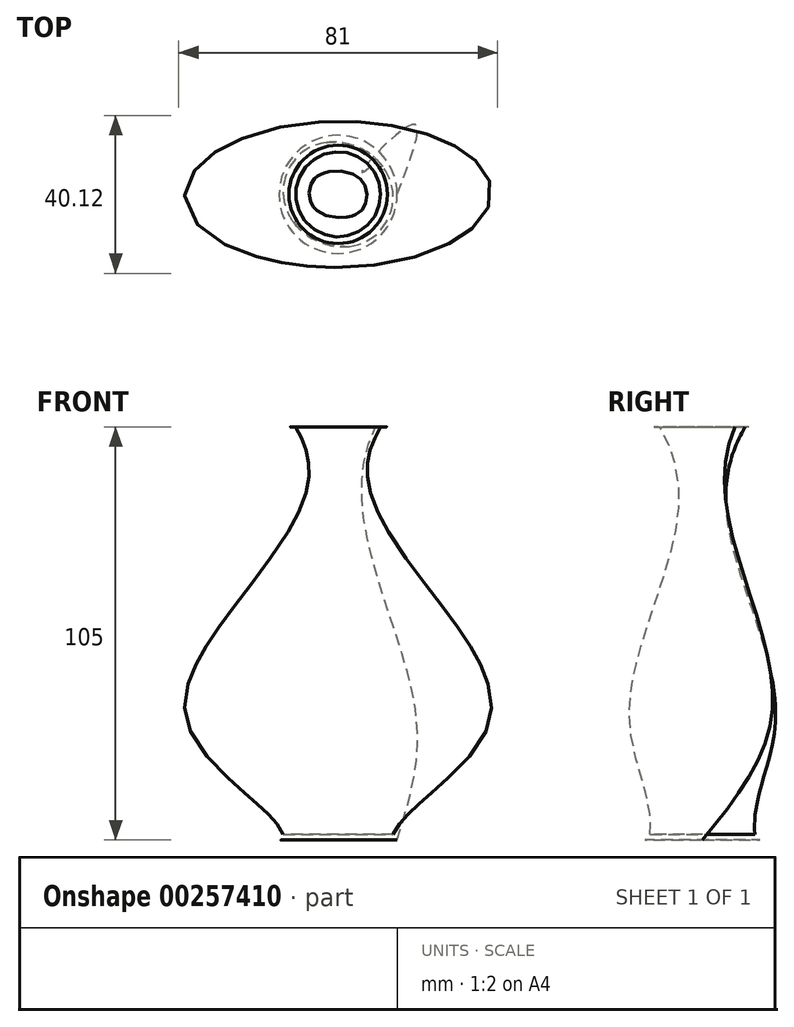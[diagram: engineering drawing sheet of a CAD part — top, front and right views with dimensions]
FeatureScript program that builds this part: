
annotation { "Feature Type Name" : "Feature", "Feature Type Description" : "" }
export const myFeature = defineFeature(function(context is Context, id is Id, definition is map)
    precondition{}
    {
        {
            var Q0;
            Q0=qCreatedBy(makeId("Top.planeOp"),FACE);
            var sketch = newSketch(context, id + "F0", { "sketchPlane" : qUnion([Q0])});
            skLineSegment(sketch, "E0", {"start": v(0, 39.05) * mm, "end": v(0, -38.03) * mm, "construction": true});
            skLineSegment(sketch, "E1", {"start": v(-37.1, 0) * mm, "end": v(37.44, 0) * mm, "construction": true});
            skCircle(sketch, "E2", {"center": v(0, 0) * mm, "radius": 15 * mm});
            skSolve(sketch);
        }
        {
            var Q0;
            Q0=qCreatedBy(makeId("Top.planeOp"),FACE);
            cPlane(context, id + "F1", {"entities" : qUnion([Q0]), "cplaneType" : CPlaneType.OFFSET, "offset" : 30 * mm, "width" : 150 * mm, "height" : 150 * mm});
        }
        {
            var Q0;
            Q0=qCreatedBy(id+"F1.planeOp",FACE);
            var sketch = newSketch(context, id + "F2", { "sketchPlane" : qUnion([Q0])});
            skEllipse(sketch, "E3", {"center": v(0, 0) * mm, "majorRadius": 40 * mm, "minorRadius": 20 * mm, "majorAxis": v(1, 0)});
            skSolve(sketch);
        }
        {
            var Q0;
            Q0=qCreatedBy(makeId("Top.planeOp"),FACE);
            cPlane(context, id + "F3", {"entities" : qUnion([Q0]), "cplaneType" : CPlaneType.OFFSET, "offset" : 100 * mm, "width" : 150 * mm, "height" : 150 * mm});
        }
        {
            var Q0;
            Q0=qCreatedBy(id+"F3.planeOp",FACE);
            var sketch = newSketch(context, id + "F4", { "sketchPlane" : qUnion([Q0])});
            skCircle(sketch, "E4", {"center": v(0, 0) * mm, "radius": 10 * mm});
            skSolve(sketch);
        }
        {
            var Q0;
            Q0=qCreatedBy(makeId("Top.planeOp"),FACE);
            cPlane(context, id + "F5", {"entities" : qUnion([Q0]), "cplaneType" : CPlaneType.OFFSET, "offset" : 105 * mm, "width" : 150 * mm, "height" : 150 * mm});
        }
        {
            var Q0;
            Q0=qCreatedBy(id+"F5.planeOp",FACE);
            var sketch = newSketch(context, id + "F6", { "sketchPlane" : qUnion([Q0])});
            skCircle(sketch, "E5", {"center": v(0, 0) * mm, "radius": 12.5 * mm});
            skSolve(sketch);
        }
        {
            var Q0;
            Q0=makeQuery(id+"F0.imprint","IMPRINT",FACE,{"disambiguationData":[TD([[makeQuery(id+"F0.imprint","IMPRINT",EDGE,{"derivedFrom":sQuery(id+"F0.wireOp",EDGE,"E2")}),1.0]])]});
            var Q1;
            Q1=makeQuery(id+"F2.imprint","IMPRINT",FACE,{"disambiguationData":[TD([[makeQuery(id+"F2.imprint","IMPRINT",EDGE,{"derivedFrom":sQuery(id+"F2.wireOp",EDGE,"E3")}),1.0]])]});
            var Q2;
            Q2=makeQuery(id+"F4.imprint","IMPRINT",FACE,{"disambiguationData":[TD([[makeQuery(id+"F4.imprint","IMPRINT",EDGE,{"derivedFrom":sQuery(id+"F4.wireOp",EDGE,"E4")}),1.0]])]});
            var Q3;
            Q3=makeQuery(id+"F6.imprint","IMPRINT",FACE,{"disambiguationData":[TD([[makeQuery(id+"F6.imprint","IMPRINT",EDGE,{"derivedFrom":sQuery(id+"F6.wireOp",EDGE,"E5")}),1.0]])]});
            loft(context, id + "F7", {"sheetProfilesArray" : [{ "sheetProfileEntities" : qUnion([Q0]) }, { "sheetProfileEntities" : qUnion([Q1]) }, { "sheetProfileEntities" : qUnion([Q2]) }, { "sheetProfileEntities" : qUnion([Q3]) }]});
        }
        {
            var Q0;
            Q0=makeQuery(id+"F7.opLoft","CAP_FACE",FACE,{"disambiguationData":[OSD([makeQuery(id+"F6.imprint","IMPRINT",FACE,{"disambiguationData":[TD([[makeQuery(id+"F6.imprint","IMPRINT",EDGE,{"derivedFrom":sQuery(id+"F6.wireOp",EDGE,"E5")}),1.0]])]})])],"isStart":true});
            shell(context, id + "F8", {"entities" : qUnion([Q0]), "thickness" : 1.5 * mm});
        }
    });
